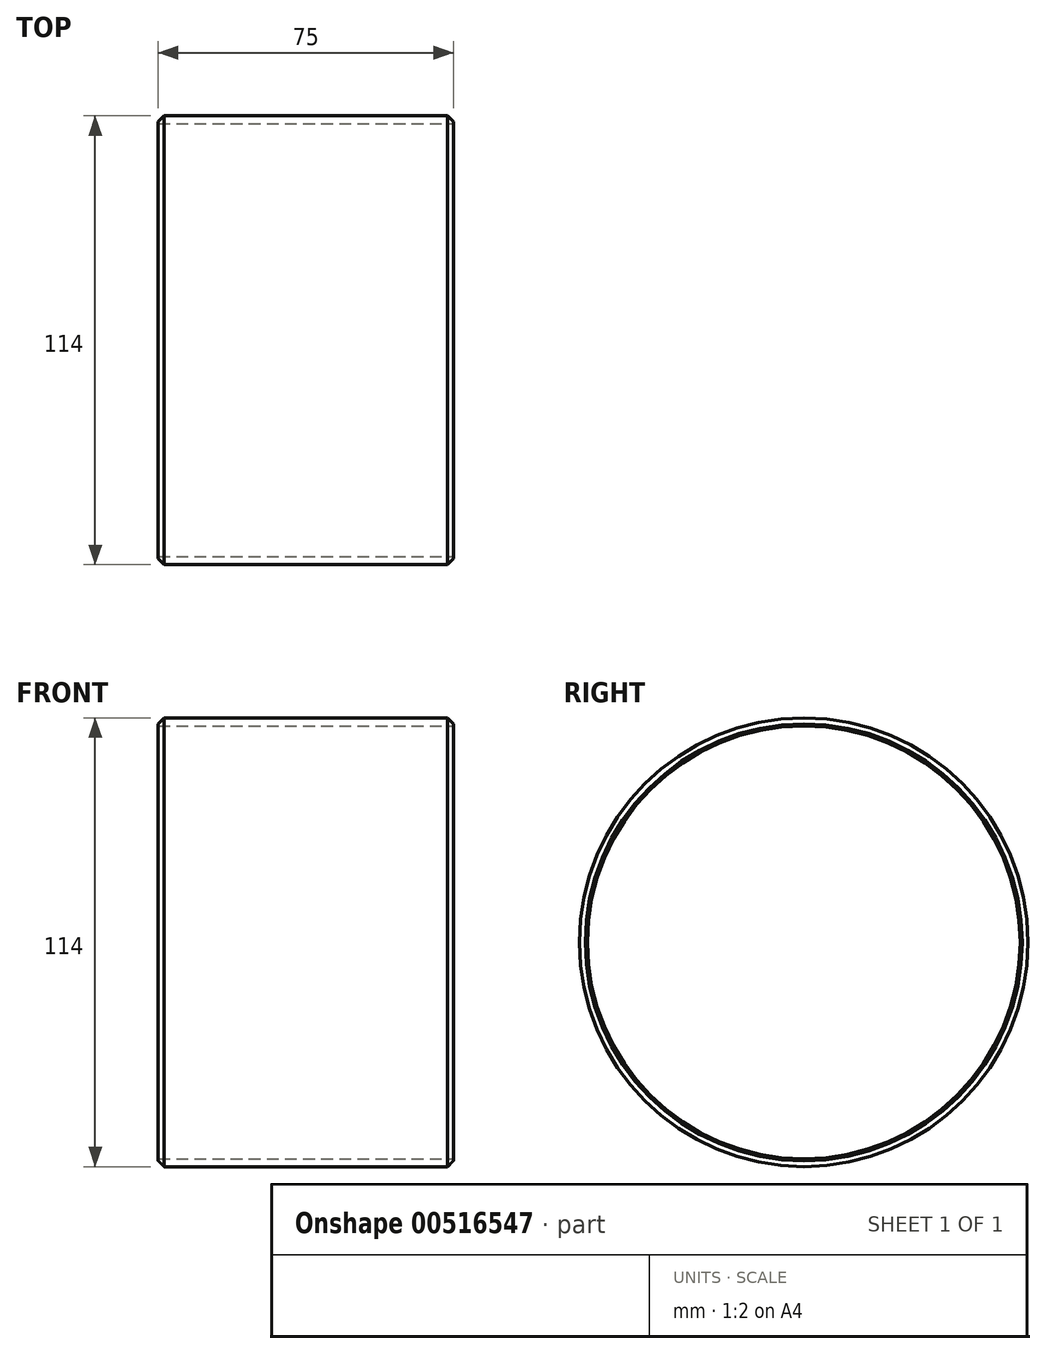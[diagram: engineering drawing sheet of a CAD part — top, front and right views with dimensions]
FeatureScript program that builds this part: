
annotation { "Feature Type Name" : "Feature", "Feature Type Description" : "" }
export const myFeature = defineFeature(function(context is Context, id is Id, definition is map)
    precondition{}
    {
        {
            var Q0;
            Q0=qCreatedBy(makeId("Front.planeOp"),FACE);
            var sketch = newSketch(context, id + "F0", { "sketchPlane" : qUnion([Q0])});
            skLineSegment(sketch, "E0", {"start": v(0, 0) * mm, "end": v(75, 0) * mm});
            skSolve(sketch);
        }
        {
            var Q0;
            Q0=qCreatedBy(makeId("Right.planeOp"),FACE);
            var sketch = newSketch(context, id + "F1", { "sketchPlane" : qUnion([Q0])});
            skCircle(sketch, "E1", {"center": v(0, 0) * mm, "radius": 55 * mm});
            skCircle(sketch, "E2", {"center": v(0, 0) * mm, "radius": 57 * mm});
            skSolve(sketch);
        }
        {
            var Q0;
            Q0=makeQuery(id+"F1.imprint","IMPRINT",FACE,{"disambiguationData":[TD([[makeQuery(id+"F1.imprint","IMPRINT",EDGE,{"derivedFrom":sQuery(id+"F1.wireOp",EDGE,"E1")}),-1.0]])]});
            var Q1;
            Q1=sQuery(id+"F0.wireOp",EDGE,"E0");
            var Q2;
            Q2=sQuery(id+"F0.wireOp",EDGE,"6f13bb82-1f5c-4c7a-b2a2-c1b73aba5f29.filletArc");
            var Q3;
            Q3=sQuery(id+"F0.wireOp",EDGE,"8xdkY1oD-0N9p-prNj-arOK-juGcHPOHZ1tJ");
            sweep(context, id + "F2", {"profiles" : qUnion([Q0]), "path" : qUnion([Q1, Q2, Q3])});
        }
        {
            var Q0;
            Q0=makeQuery(id+"F2.opSweep","CAP_EDGE",EDGE,{"disambiguationData":[OSD([sQuery(id+"F0.wireOp",VERTEX,"E0.start"),sQuery(id+"F1.wireOp",EDGE,"E2")])],"isStart":true});
            var Q1;
            Q1=makeQuery(id+"F2.opSweep","CAP_EDGE",EDGE,{"disambiguationData":[OSD([sQuery(id+"F0.wireOp",VERTEX,"E0.end"),sQuery(id+"F1.wireOp",EDGE,"E2")])],"isStart":false});
            chamfer(context, id + "F3", {"entities" : qUnion([Q0, Q1]), "width" : 1.5 * mm, "tangentPropagation" : true});
        }
    });
